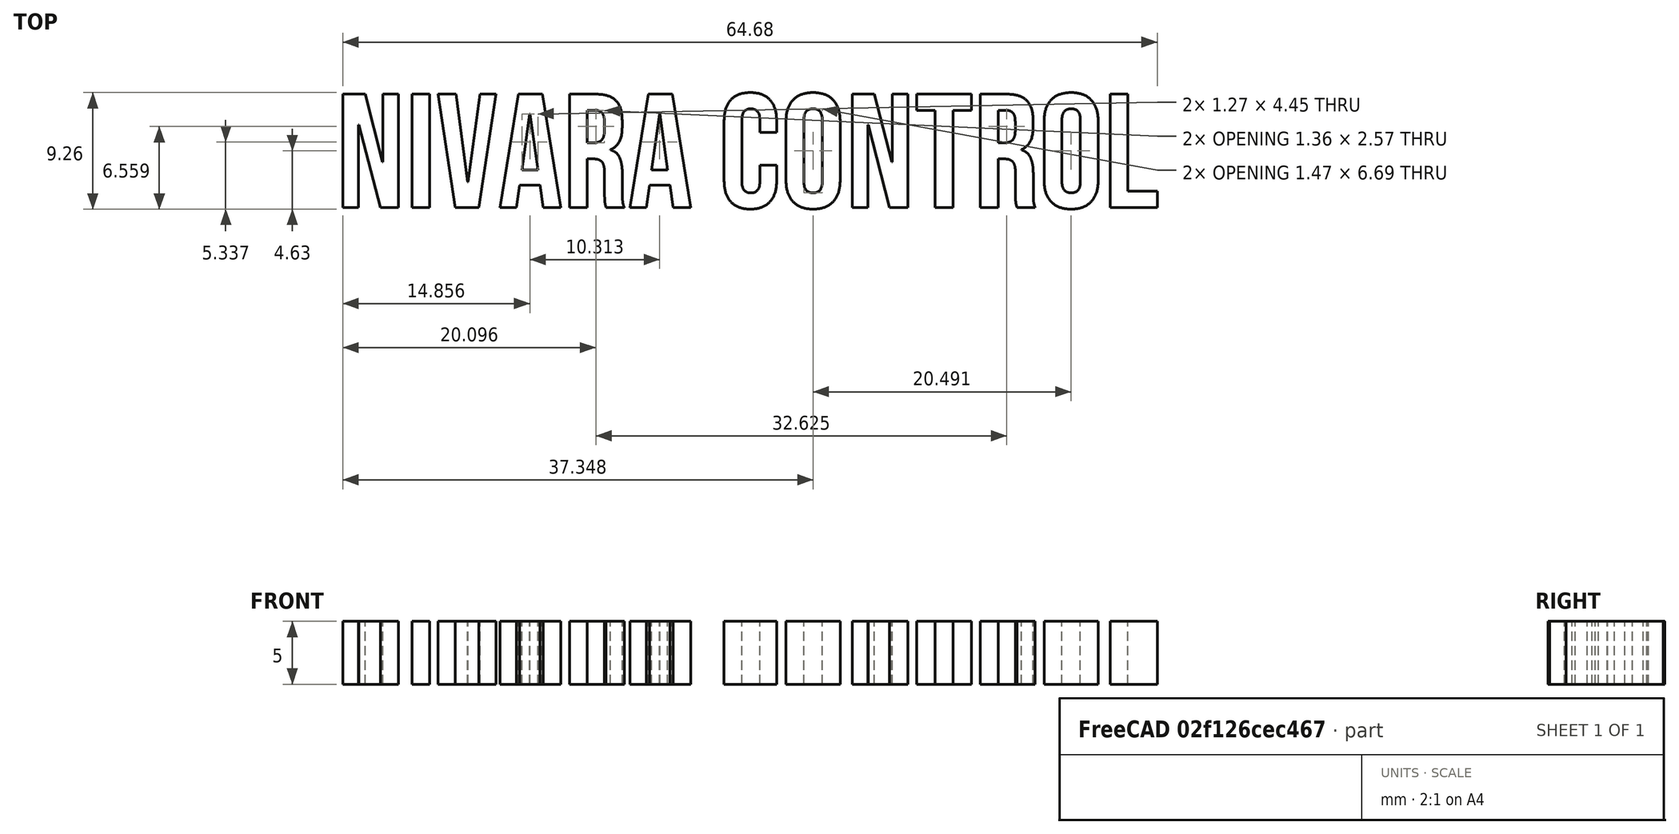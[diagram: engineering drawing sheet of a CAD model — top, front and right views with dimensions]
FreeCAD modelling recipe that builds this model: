
FCSTD DOCUMENT  (FreeCAD 1.0R39285 (Git))
Label: Logo del Proyecto (2023-1283)
License: All rights reserved
LicenseURL: https://en.wikipedia.org/wiki/All_rights_reserved
objects: Part::Box×1, Part::Part2DObjectPython×1, Part::Extrusion×1, Part::Cut×1
note: 4 computed .brp shape members not serialized (recipe doc carries the construction recipe); baked Part::Feature solids carry a one-line shape summary decoded from their .brp

FEATURE [Part::Box] Box  label="Cubo"
  AttacherType = Attacher::AttachEngine3D
  Height = 15
  Length = 75
  Placement = pos=(-30,-12,-17) rot=(0,0,1;0rad)
  Width = 40
FEATURE [Part::Part2DObjectPython] ShapeString  # Draft 2D object (typed FeaturePython)
  FontFile = <userpath>/Downloads/Bebas_Neue/BebasNeue-Regular.ttf
  Fuse = false
  Justification = 6
  JustificationReference = 0
  KeepLeftMargin = false
  MakeFace = true
  ObliqueAngle = 0
  Placement = pos=(-25,5,1) rot=(0,0,1;0rad)
  ScaleToSize = true
  Size = 9
  String = NIVARA CONTROL
  Tracking = 0
FEATURE [Part::Extrusion] Extrude
  Base = -> ShapeString
  Dir = (0,0,1)
  DirMode = 2
  FaceMakerClass = Part::FaceMakerBullseye
  FaceMakerMode = 3
  LengthFwd = 5
  LengthRev = 0
  Solid = false
  Symmetric = false
FEATURE [Part::Cut] Cut
  Base = -> Extrude
  Tool = -> Box
